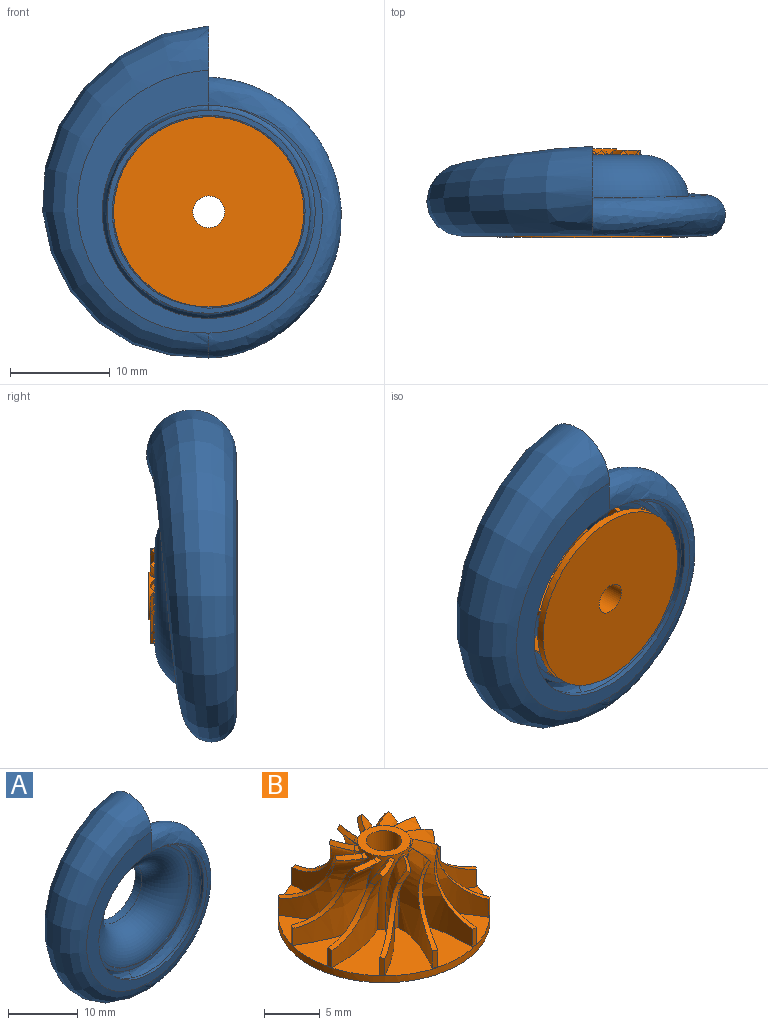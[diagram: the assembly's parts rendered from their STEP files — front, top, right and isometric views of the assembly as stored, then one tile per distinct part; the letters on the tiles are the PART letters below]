
ASSEMBLY  parts=2 mates=1
PART A: 23 faces, bbox 31.9x11.2x34.3 mm
  f0: offset ~5.71x5.7mm, area 5.7mm2, adj f4,f5,f10,f21
  f1: bspline ~19.35x9.96mm, area 3.9mm2, adj f2,f19,f21
  f2: bspline ~19.59x10.1mm, area 3.9mm2, adj f1,f19,f21
  f3: offset ~29.11x14.8mm, area 284.6mm2, adj f4,f10,f13,f14,f21,f22
  f4: cylinder r=10.16mm len=5.06mm, axis (0,-1,0), area 6.7mm2, adj f0,f3,f10,f21
  f5: cylinder r=10.16mm len=17.34mm, axis (0,-1,0), area 31.8mm2, adj f0,f8,f9,f10,f13,f16,f20,f21
  f6: plane 9.13x9.13mm, normal (1,0,0), area 11.5mm2, adj f7,f8,f9,f10,f11,f12,f14,f20
  f7: bspline ~12.96x9.65mm, area 8.8mm2, adj f6,f11,f17
  f8: bspline ~28.1x13.29mm, area 329.9mm2, adj f5,f6,f11,f12,f13,f20,f22
  f9: offset ~13.97x10.67mm, area 10.1mm2, adj f5,f6,f10,f16
  f10: offset ~34.26x18.23mm, area 612.4mm2, adj f0,f3,f4,f5,f6,f9,f14,f16
  f11: bspline ~33.25x17.22mm, area 718.1mm2, adj f6,f7,f8,f12,f15,f17,f20
  f12: plane 26.45x24.75mm, normal (0,-1,0), area 117.3mm2, adj f6,f8,f11,f22
  f13: plane 3.57x3.57mm, normal (-1,0,0), area 3mm2, adj f3,f5,f8,f14
  f14: plane 26.45x24.75mm, normal (0,1,0), area 117.3mm2, adj f3,f6,f10,f13,f22
  f15: plane 5.28x4.95mm, normal (0,1,0), area 0.3mm2, adj f11,f17
  f16: plane 4.23x0.93mm, normal (0,1,0), area 0mm2, adj f5,f9,f10
  f17: torus R=4.89mm, axis (0,-1,0), area 370.3mm2, adj f7,f11,f15,f18,f20
  f18: cylinder r=4.89mm len=9.78mm, axis (0,-1,0), area 41mm2, adj f17,f19
  f19: torus R=9.65mm, axis (0,-1,0), area 310.8mm2, adj f1,f2,f18
  f20: plane 20.27x11.64mm, normal (0,1,0), area 11.3mm2, adj f5,f6,f8,f11,f17
  f21: plane 20.48x20.48mm, normal (0,-1,0), area 32mm2, adj f0,f1,f2,f3,f4,f5
  f22: cylinder r=10.67mm len=21.34mm, axis (0,-1,0), area 34.1mm2, adj f3,f8,f12,f14
PART B: 138 faces, bbox 20.9x20.9x9.9 mm
  f0: bspline ~7.62x2.38mm, area 0.5mm2, adj f48,f51,f136
  f1: offset ~8.62x3.38mm, area 0.2mm2, adj f3,f52,f137
  f2: offset ~8.62x3.38mm, area 0.3mm2, adj f48,f52,f136
  f3: plane 7.3x6.32mm, normal (0,0,1), area 18.7mm2, adj f1,f49,f52,f128,f132,f137
  f4: bspline ~7.62x2.81mm, area 0.5mm2, adj f55,f128,f136,f137
  f5: bspline ~7.62x2.81mm, area 0.5mm2, adj f56,f59,f136
  f6: offset ~8.62x3.81mm, area 0.2mm2, adj f8,f60,f136
  f7: offset ~2.78x2.03mm, area 0.3mm2, adj f56,f60,f136
  f8: plane 7.4x5.07mm, normal (0,0,1), area 18.7mm2, adj f6,f51,f57,f60,f132,f136
  f9: bspline ~7.62x2.81mm, area 0.5mm2, adj f63,f66,f136
  f10: offset ~8.62x3.81mm, area 0.2mm2, adj f12,f67,f136
  f11: offset ~8.62x3.81mm, area 0.3mm2, adj f63,f67,f136
  f12: plane 7.72x5.74mm, normal (0,0,1), area 18.7mm2, adj f10,f59,f64,f67,f132,f136
  f13: bspline ~7.62x2.38mm, area 0.5mm2, adj f70,f73,f136
  f14: offset ~8.62x3.38mm, area 0.2mm2, adj f16,f74,f136
  f15: offset ~8.62x3.38mm, area 0.3mm2, adj f70,f74,f136
  f16: plane 7.3x6.32mm, normal (0,0,1), area 18.7mm2, adj f14,f66,f71,f74,f132,f136
  f17: bspline ~7.62x2.81mm, area 0.5mm2, adj f77,f80,f136
  f18: offset ~8.62x3.81mm, area 0.2mm2, adj f20,f81,f136
  f19: offset ~2.78x2.03mm, area 0.3mm2, adj f77,f81,f136
  f20: plane 7.4x5.07mm, normal (0,0,1), area 18.6mm2, adj f18,f73,f78,f81,f132,f136
  f21: bspline ~7.62x2.81mm, area 0.5mm2, adj f84,f87,f136
  f22: offset ~8.62x3.81mm, area 0.2mm2, adj f24,f88,f136
  f23: offset ~8.62x3.81mm, area 0.3mm2, adj f84,f88,f136
  f24: plane 7.72x5.74mm, normal (0,0,1), area 18.6mm2, adj f22,f80,f85,f88,f132,f136
  f25: bspline ~7.62x2.38mm, area 0.5mm2, adj f91,f94,f136
  f26: offset ~8.62x3.38mm, area 0.2mm2, adj f28,f95,f136
  f27: offset ~8.62x3.38mm, area 0.3mm2, adj f91,f95,f136
  f28: plane 7.3x6.32mm, normal (0,0,1), area 18.7mm2, adj f26,f87,f92,f95,f132,f136
  f29: bspline ~7.62x2.81mm, area 0.5mm2, adj f98,f101,f136
  f30: offset ~8.62x3.81mm, area 0.2mm2, adj f32,f102,f136
  f31: offset ~2.78x2.03mm, area 0.3mm2, adj f98,f102,f136
  f32: plane 7.4x5.07mm, normal (0,0,1), area 18.7mm2, adj f30,f94,f99,f102,f132,f136
  f33: bspline ~7.62x2.81mm, area 0.5mm2, adj f105,f108,f136
  f34: offset ~8.62x3.81mm, area 0.2mm2, adj f36,f109,f136
  f35: offset ~8.62x3.81mm, area 0.3mm2, adj f105,f109,f136
  f36: plane 7.72x5.74mm, normal (0,0,1), area 18.7mm2, adj f34,f101,f106,f109,f132,f136
  f37: bspline ~7.62x2.38mm, area 0.5mm2, adj f112,f115,f136
  f38: offset ~8.62x3.38mm, area 0.2mm2, adj f40,f116,f136
  f39: offset ~8.62x3.38mm, area 0.3mm2, adj f112,f116,f136
  f40: plane 7.3x6.32mm, normal (0,0,1), area 18.6mm2, adj f38,f108,f113,f116,f132,f136
  f41: bspline ~7.62x2.81mm, area 0.5mm2, adj f119,f122,f136
  f42: offset ~8.62x3.81mm, area 0.2mm2, adj f44,f123,f136
  f43: offset ~2.78x2.03mm, area 0.3mm2, adj f119,f123,f136
  f44: plane 7.4x5.07mm, normal (0,0,1), area 18.6mm2, adj f42,f115,f120,f123,f132,f136
  f45: offset ~8.62x3.81mm, area 0.2mm2, adj f47,f129,f136
  f46: offset ~8.62x3.81mm, area 0.3mm2, adj f55,f129,f136
  f47: plane 7.72x5.74mm, normal (0,0,1), area 18.6mm2, adj f45,f122,f126,f129,f132,f136
  f48: plane 0.54x0.36mm, normal (0,0.71,0.71), area 0.2mm2, adj f0,f2,f50,f136
  f49: bspline ~1.94x0.44mm, area 1mm2, adj f3,f51,f52,f54
  f50: bspline ~2.47x0.66mm, area 1.2mm2, adj f48,f51,f52,f53
  f51: bspline ~7.62x7.59mm, area 33.8mm2, adj f0,f8,f49,f50,f53,f54
  f52: offset ~8.62x8.59mm, area 34.3mm2, adj f1,f2,f3,f49,f50,f53,f54
  f53: plane 1.33x1.31mm, normal (1,0,0), area 0.7mm2, adj f50,f51,f52,f54
  f54: cylinder r=4.76mm len=4.75mm, axis (0,1,0), area 3.9mm2, adj f49,f51,f52,f53
  f55: plane 0.58x0.47mm, normal (0.35,0.61,0.71), area 0.2mm2, adj f4,f46,f127,f136
  f56: plane 0.65x0.46mm, normal (-0.35,0.61,0.71), area 0.2mm2, adj f5,f7,f58,f136
  f57: bspline ~3.2x0.55mm, area 1mm2, adj f8,f59,f60,f62
  f58: bspline ~2.39x1.27mm, area 1.2mm2, adj f56,f59,f60,f61
  f59: bspline ~7.87x7.62mm, area 33.8mm2, adj f5,f12,f57,f58,f61,f62
  f60: offset ~8.87x8.62mm, area 34.3mm2, adj f6,f7,f8,f57,f58,f61,f62
  f61: plane 1.33x1.14mm, normal (0.87,0.5,0), area 0.7mm2, adj f58,f59,f60,f62
  f62: cylinder r=4.76mm len=5.52mm, axis (-0.5,0.87,0), area 3.9mm2, adj f57,f59,f60,f61
  f63: plane 0.58x0.47mm, normal (-0.61,0.35,0.71), area 0.2mm2, adj f9,f11,f65,f136
  f64: bspline ~3.2x0.47mm, area 1mm2, adj f12,f66,f67,f69
  f65: bspline ~4.15x4.03mm, area 1.2mm2, adj f63,f66,f67,f68
  f66: bspline ~7.62x6.79mm, area 33.8mm2, adj f9,f16,f64,f65,f68,f69
  f67: offset ~8.62x7.79mm, area 34.3mm2, adj f10,f11,f12,f64,f65,f68,f69
  f68: plane 1.33x1.14mm, normal (0.5,0.87,0), area 0.7mm2, adj f65,f66,f67,f69
  f69: cylinder r=4.76mm len=5.52mm, axis (-0.87,0.5,0), area 3.9mm2, adj f64,f66,f67,f68
  f70: plane 0.54x0.36mm, normal (-0.71,0,0.71), area 0.2mm2, adj f13,f15,f72,f136
  f71: bspline ~1.94x0.44mm, area 1mm2, adj f16,f73,f74,f76
  f72: bspline ~2.47x0.66mm, area 1.2mm2, adj f70,f73,f74,f75
  f73: bspline ~7.62x7.59mm, area 33.8mm2, adj f13,f20,f71,f72,f75,f76
  f74: offset ~8.62x8.59mm, area 34.3mm2, adj f14,f15,f16,f71,f72,f75,f76
  f75: plane 1.33x1.31mm, normal (0,1,0), area 0.7mm2, adj f72,f73,f74,f76
  f76: cylinder r=4.76mm len=4.75mm, axis (-1,0,0), area 3.9mm2, adj f71,f73,f74,f75
  f77: plane 0.65x0.46mm, normal (-0.61,-0.35,0.71), area 0.2mm2, adj f17,f19,f79,f136
  f78: bspline ~3.2x0.55mm, area 1mm2, adj f20,f80,f81,f83
  f79: bspline ~2.39x1.27mm, area 1.2mm2, adj f77,f80,f81,f82
  f80: bspline ~7.87x7.62mm, area 33.8mm2, adj f17,f24,f78,f79,f82,f83
  f81: offset ~8.87x8.62mm, area 34.3mm2, adj f18,f19,f20,f78,f79,f82,f83
  f82: plane 1.33x1.14mm, normal (-0.5,0.87,0), area 0.7mm2, adj f79,f80,f81,f83
  f83: cylinder r=4.76mm len=5.52mm, axis (-0.87,-0.5,0), area 3.9mm2, adj f78,f80,f81,f82
  f84: plane 0.58x0.47mm, normal (-0.35,-0.61,0.71), area 0.2mm2, adj f21,f23,f86,f136
  f85: bspline ~3.2x0.47mm, area 1mm2, adj f24,f87,f88,f90
  f86: bspline ~4.15x4.03mm, area 1.2mm2, adj f84,f87,f88,f89
  f87: bspline ~7.62x6.79mm, area 33.8mm2, adj f21,f28,f85,f86,f89,f90
  f88: offset ~8.62x7.79mm, area 34.3mm2, adj f22,f23,f24,f85,f86,f89,f90
  f89: plane 1.33x1.14mm, normal (-0.87,0.5,0), area 0.7mm2, adj f86,f87,f88,f90
  f90: cylinder r=4.76mm len=5.52mm, axis (-0.5,-0.87,0), area 3.9mm2, adj f85,f87,f88,f89
  f91: plane 0.54x0.36mm, normal (0,-0.71,0.71), area 0.2mm2, adj f25,f27,f93,f136
  f92: bspline ~1.94x0.44mm, area 1mm2, adj f28,f94,f95,f97
  f93: bspline ~2.47x0.66mm, area 1.2mm2, adj f91,f94,f95,f96
  f94: bspline ~7.62x7.59mm, area 33.8mm2, adj f25,f32,f92,f93,f96,f97
  f95: offset ~8.62x8.59mm, area 34.3mm2, adj f26,f27,f28,f92,f93,f96,f97
  f96: plane 1.33x1.31mm, normal (-1,0,0), area 0.7mm2, adj f93,f94,f95,f97
  f97: cylinder r=4.76mm len=4.75mm, axis (0,-1,0), area 3.9mm2, adj f92,f94,f95,f96
  f98: plane 0.65x0.46mm, normal (0.35,-0.61,0.71), area 0.2mm2, adj f29,f31,f100,f136
  f99: bspline ~3.2x0.55mm, area 1mm2, adj f32,f101,f102,f104
  f100: bspline ~2.39x1.27mm, area 1.2mm2, adj f98,f101,f102,f103
  f101: bspline ~7.87x7.62mm, area 33.8mm2, adj f29,f36,f99,f100,f103,f104
  f102: offset ~8.87x8.62mm, area 34.3mm2, adj f30,f31,f32,f99,f100,f103,f104
  f103: plane 1.33x1.14mm, normal (-0.87,-0.5,0), area 0.7mm2, adj f100,f101,f102,f104
  f104: cylinder r=4.76mm len=5.52mm, axis (0.5,-0.87,0), area 3.9mm2, adj f99,f101,f102,f103
  f105: plane 0.58x0.47mm, normal (0.61,-0.35,0.71), area 0.2mm2, adj f33,f35,f107,f136
  f106: bspline ~3.2x0.47mm, area 1mm2, adj f36,f108,f109,f111
  f107: bspline ~4.15x4.03mm, area 1.2mm2, adj f105,f108,f109,f110
  f108: bspline ~7.62x6.79mm, area 33.8mm2, adj f33,f40,f106,f107,f110,f111
  f109: offset ~8.62x7.79mm, area 34.3mm2, adj f34,f35,f36,f106,f107,f110,f111
  f110: plane 1.33x1.14mm, normal (-0.5,-0.87,0), area 0.7mm2, adj f107,f108,f109,f111
  f111: cylinder r=4.76mm len=5.52mm, axis (0.87,-0.5,0), area 3.9mm2, adj f106,f108,f109,f110
  f112: plane 0.54x0.36mm, normal (0.71,0,0.71), area 0.2mm2, adj f37,f39,f114,f136
  f113: bspline ~1.94x0.44mm, area 1mm2, adj f40,f115,f116,f118
  f114: bspline ~2.47x0.66mm, area 1.2mm2, adj f112,f115,f116,f117
  f115: bspline ~7.62x7.59mm, area 33.8mm2, adj f37,f44,f113,f114,f117,f118
  f116: offset ~8.62x8.59mm, area 34.3mm2, adj f38,f39,f40,f113,f114,f117,f118
  f117: plane 1.33x1.31mm, normal (0,-1,0), area 0.7mm2, adj f114,f115,f116,f118
  f118: cylinder r=4.76mm len=4.75mm, axis (1,0,0), area 3.9mm2, adj f113,f115,f116,f117
  f119: plane 0.65x0.46mm, normal (0.61,0.35,0.71), area 0.2mm2, adj f41,f43,f121,f136
  f120: bspline ~3.2x0.55mm, area 1mm2, adj f44,f122,f123,f125
  f121: bspline ~2.39x1.27mm, area 1.2mm2, adj f119,f122,f123,f124
  f122: bspline ~7.87x7.62mm, area 33.8mm2, adj f41,f47,f120,f121,f124,f125
  f123: offset ~8.87x8.62mm, area 34.3mm2, adj f42,f43,f44,f120,f121,f124,f125
  f124: plane 1.33x1.14mm, normal (0.5,-0.87,0), area 0.7mm2, adj f121,f122,f123,f125
  f125: cylinder r=4.76mm len=5.52mm, axis (0.87,0.5,0), area 3.9mm2, adj f120,f122,f123,f124
  f126: bspline ~3.2x0.47mm, area 1mm2, adj f47,f128,f129,f131
  f127: bspline ~4.15x4.03mm, area 1.2mm2, adj f55,f128,f129,f130
  f128: bspline ~7.62x6.79mm, area 33.8mm2, adj f3,f4,f126,f127,f130,f131
  f129: offset ~8.62x7.79mm, area 34.3mm2, adj f45,f46,f47,f126,f127,f130,f131
  f130: plane 1.33x1.14mm, normal (0.87,-0.5,0), area 0.7mm2, adj f127,f128,f129,f131
  f131: cylinder r=4.76mm len=5.52mm, axis (0.5,0.87,0), area 3.9mm2, adj f126,f128,f129,f130
  f132: cylinder r=9.53mm len=19.05mm, axis (0,0,1), area 45.6mm2, adj f3,f8,f12,f16,f20,f24,f28,f32
  f133: cylinder r=1.59mm len=8.89mm, axis (0,0,1), area 88.7mm2, adj f134,f135
  f134: plane 19.05x19.05mm, normal (0,0,-1), area 277.1mm2, adj f132,f133
  f135: plane 4.76x4.76mm, normal (0,0,1), area 9.9mm2, adj f133,f136
  f136: cylinder r=2.38mm len=8.13mm, axis (0,0,-1), area 66.7mm2, adj f0,f2,f4,f5,f6,f7,f8,f9
  f137: cylinder r=2.38mm len=7.27mm, axis (0,0,-1), area 5.8mm2, adj f1,f3,f4,f136
PLACE A t=(4.89,6.38,12.03)mm
PLACE B rot(axis=(-1,0,0),90deg) t=(4.89,7.02,12.03)mm
MATE revolute B.f132 <-> A.f4  axis (0,1,0) through (4.89,6.64,12.03)mm
